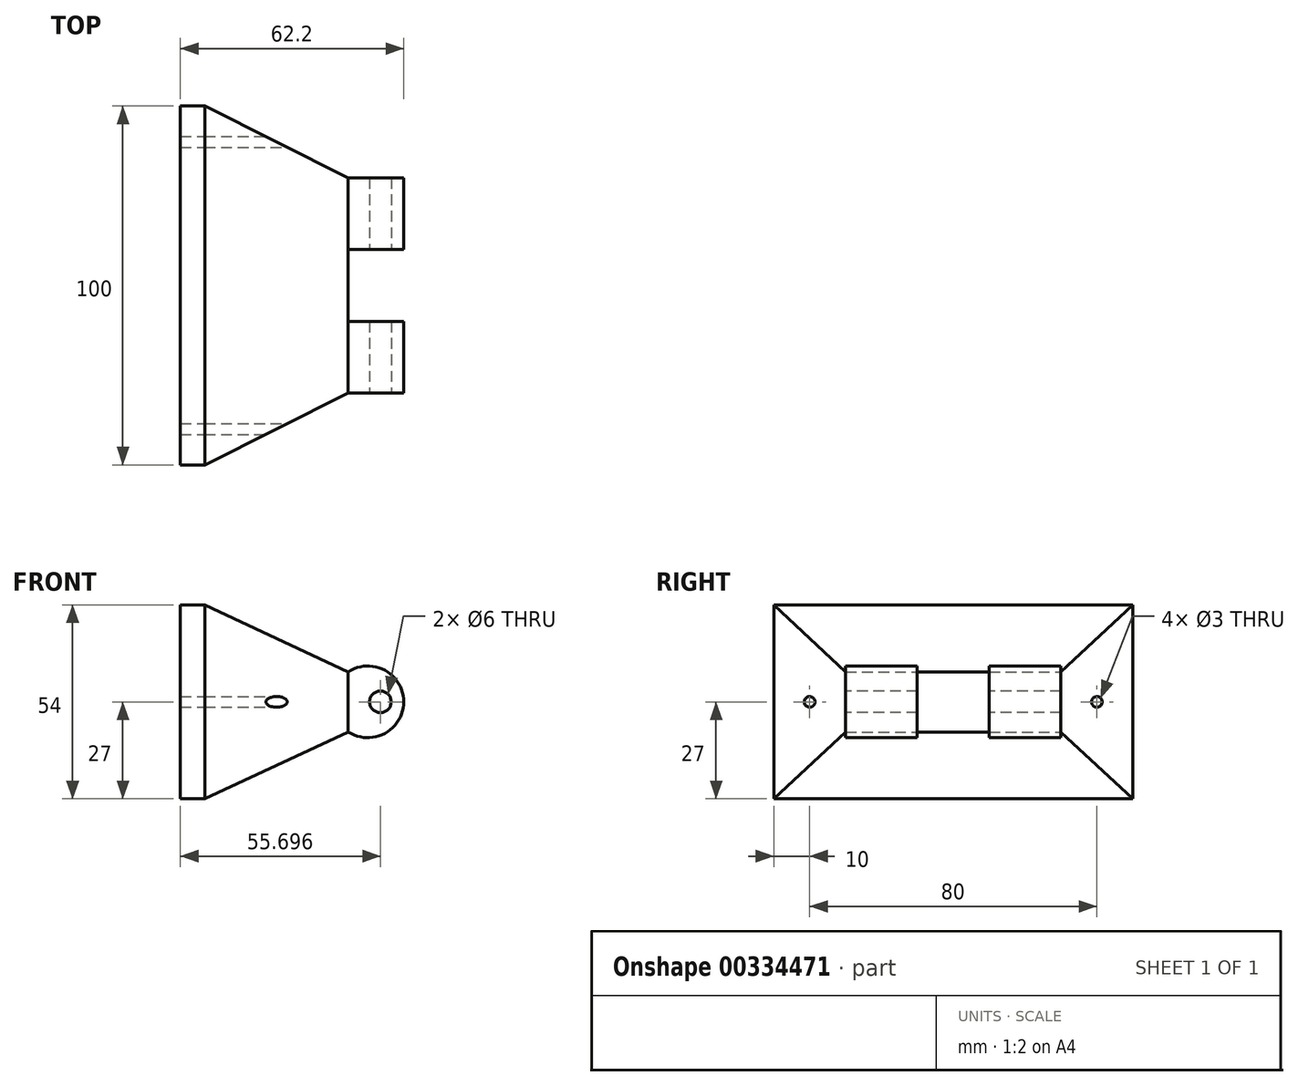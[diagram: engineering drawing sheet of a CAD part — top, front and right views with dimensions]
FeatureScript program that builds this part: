
annotation { "Feature Type Name" : "Feature", "Feature Type Description" : "" }
export const myFeature = defineFeature(function(context is Context, id is Id, definition is map)
    precondition{}
    {
        {
            var Q0;
            Q0=qCreatedBy(makeId("Front.planeOp"),FACE);
            var sketch = newSketch(context, id + "F0", { "sketchPlane" : qUnion([Q0])});
            skArc(sketch, "E0", {"start": v(0, -8.39) * mm, "mid": v(15.45, 0) * mm, "end": v(0, 8.39) * mm});
            skLineSegment(sketch, "E1", {"start": v(0, 8.39) * mm, "end": v(0, -8.39) * mm});
            skSolve(sketch);
        }
        {
            var Q0;
            Q0=makeQuery(id+"F0.imprint","IMPRINT",FACE,{"disambiguationData":[TD([[makeQuery(id+"F0.imprint","IMPRINT",EDGE,{"derivedFrom":sQuery(id+"F0.wireOp",EDGE,"E0")}),1.0]])]});
            extrude(context, id + "F1", {"entities" : qUnion([Q0]), "endBound" : BoundingType.SYMMETRIC, "depth" : 60 * mm, "offsetDistance" : 25 * mm});
        }
        {
            var Q0;
            Q0=qCreatedBy(makeId("Front.planeOp"),FACE);
            var sketch = newSketch(context, id + "F2", { "sketchPlane" : qUnion([Q0])});
            skLineSegment(sketch, "E2.top", {"start": v(-46.75, 27) * mm, "end": v(-40, 27) * mm});
            skLineSegment(sketch, "E2.left", {"start": v(-46.75, 0) * mm, "end": v(-46.75, 27) * mm});
            skLineSegment(sketch, "E2.right", {"start": v(-40, 0) * mm, "end": v(-40, 27) * mm});
            skLineSegment(sketch, "E3.top", {"start": v(-46.75, -27) * mm, "end": v(-40, -27) * mm});
            skLineSegment(sketch, "E3.left", {"start": v(-46.75, 0) * mm, "end": v(-46.75, -27) * mm});
            skLineSegment(sketch, "E3.right", {"start": v(-40, 0) * mm, "end": v(-40, -27) * mm});
            skSolve(sketch);
        }
        {
            var Q0;
            Q0=makeQuery(id+"F2.imprint","IMPRINT",FACE,{"disambiguationData":[TD([[makeQuery(id+"F2.imprint","IMPRINT",EDGE,{"derivedFrom":sQuery(id+"F2.wireOp",EDGE,"E2.top")}),-1.0]])]});
            extrude(context, id + "F3", {"entities" : qUnion([Q0]), "endBound" : BoundingType.SYMMETRIC, "depth" : 100 * mm, "offsetDistance" : 25 * mm});
        }
        {
            var Q0;
            Q0=makeQuery(id+"F3.opExtrude","SWEPT_FACE",FACE,{"disambiguationData":[OSD([sQuery(id+"F2.wireOp",EDGE,"E2.right"),sQuery(id+"F2.wireOp",EDGE,"E3.right")])]});
            var Q1;
            Q1=makeQuery(id+"F1.opExtrude","SWEPT_FACE",FACE,{"disambiguationData":[OSD([sQuery(id+"F0.wireOp",EDGE,"E1")])]});
            loft(context, id + "F4", {"sheetProfilesArray" : [{ "sheetProfileEntities" : qUnion([Q0]) }, { "sheetProfileEntities" : qUnion([Q1]) }]});
        }
        {
            var Q0;
            Q0=makeQuery(id+"F1.opExtrude","CAP_FACE",FACE,{"disambiguationData":[OSD([sQuery(id+"F0.wireOp",EDGE,"E0"),sQuery(id+"F0.wireOp",EDGE,"E1")])],"isStart":false});
            var sketch = newSketch(context, id + "F5", { "sketchPlane" : qUnion([Q0])});
            skCircle(sketch, "E4", {"center": v(8.95, 0) * mm, "radius": 3 * mm});
            skSolve(sketch);
        }
        {
            var Q0;
            Q0=qCreatedBy(makeId("Top.planeOp"),FACE);
            var sketch = newSketch(context, id + "F6", { "sketchPlane" : qUnion([Q0])});
            skLineSegment(sketch, "E5.bottom", {"start": v(0, 10) * mm, "end": v(24, 10) * mm});
            skLineSegment(sketch, "E5.top", {"start": v(0, -10) * mm, "end": v(24, -10) * mm});
            skLineSegment(sketch, "E5.left", {"start": v(0, 10) * mm, "end": v(0, -10) * mm});
            skLineSegment(sketch, "E5.right", {"start": v(24, 10) * mm, "end": v(24, -10) * mm});
            skSolve(sketch);
        }
        {
            var Q0;
            Q0 = qSketchRegion(id + "F6", true);
            extrude(context, id + "F7", {"entities" : qUnion([Q0]), "operationType" : NewBodyOperationType.REMOVE, "endBound" : BoundingType.SYMMETRIC, "oppositeDirection" : true, "depth" : 33 * mm});
        }
        {
            var Q0;
            Q0=qCreatedBy(makeId("Right.planeOp"),FACE);
            var sketch = newSketch(context, id + "F8", { "sketchPlane" : qUnion([Q0])});
            skLineSegment(sketch, "E6", {"start": v(0, 0) * mm, "end": v(-40, 0) * mm});
            skLineSegment(sketch, "E7", {"start": v(0, 0) * mm, "end": v(40, 0) * mm});
            skCircle(sketch, "E8", {"center": v(-40, 0) * mm, "radius": 1.5 * mm});
            skCircle(sketch, "E9", {"center": v(40, 0) * mm, "radius": 1.5 * mm});
            skSolve(sketch);
        }
        {
            var Q0;
            Q0=sQuery(id+"F8.wireOp",VERTEX,"E6.end");
            var Q1;
            Q1=sQuery(id+"F8.wireOp",VERTEX,"E7.end");
            var Q2;
            Q2=makeQuery(id+"F3.opExtrude","SWEPT_BODY",BODY,{"disambiguationData":[OSD([sQuery(id+"F2.wireOp",EDGE,"E2.top"),sQuery(id+"F2.wireOp",EDGE,"E2.left"),sQuery(id+"F2.wireOp",EDGE,"E2.right"),sQuery(id+"F2.wireOp",EDGE,"E3.top"),sQuery(id+"F2.wireOp",EDGE,"E3.left"),sQuery(id+"F2.wireOp",EDGE,"E3.right")])]});
            var Q3;
            Q3=makeQuery(id+"F4.opLoft","SWEPT_BODY",BODY,{"disambiguationData":[OSD([sQuery(id+"F0.wireOp",EDGE,"E1"),sQuery(id+"F2.wireOp",EDGE,"E2.right"),sQuery(id+"F2.wireOp",EDGE,"E3.right")])]});
            hole(context, id + "F9", {"style" : HoleStyle.SIMPLE, "endStyle" : HoleEndStyle.THROUGH, "holeDiameter" : 3 * mm, "isTappedThrough" : true, "tappedDepth" : 12 * mm, "tapClearance" : 3, "locations" : qUnion([Q0, Q1]), "scope" : qUnion([Q2, Q3])});
        }
        {
            var Q0;
            Q0=sQuery(id+"F5.wireOp",VERTEX,"E4.center");
            var Q1;
            Q1=makeQuery(id+"F7.boolean.opBoolean","SPLIT",BODY,{"disambiguationData":[OD(0.0)],"derivedFrom":makeQuery(id+"F1.opExtrude","SWEPT_BODY",BODY,{"disambiguationData":[OSD([sQuery(id+"F0.wireOp",EDGE,"E0"),sQuery(id+"F0.wireOp",EDGE,"E1")])]})});
            var Q2;
            Q2=makeQuery(id+"F7.boolean.opBoolean","SPLIT",BODY,{"disambiguationData":[OD(1.0)],"derivedFrom":makeQuery(id+"F1.opExtrude","SWEPT_BODY",BODY,{"disambiguationData":[OSD([sQuery(id+"F0.wireOp",EDGE,"E0"),sQuery(id+"F0.wireOp",EDGE,"E1")])]})});
            hole(context, id + "F10", {"style" : HoleStyle.SIMPLE, "endStyle" : HoleEndStyle.THROUGH, "holeDiameter" : 6 * mm, "isTappedThrough" : true, "tappedDepth" : 12 * mm, "tapClearance" : 3, "locations" : qUnion([Q0]), "scope" : qUnion([Q1, Q2])});
        }
    });
